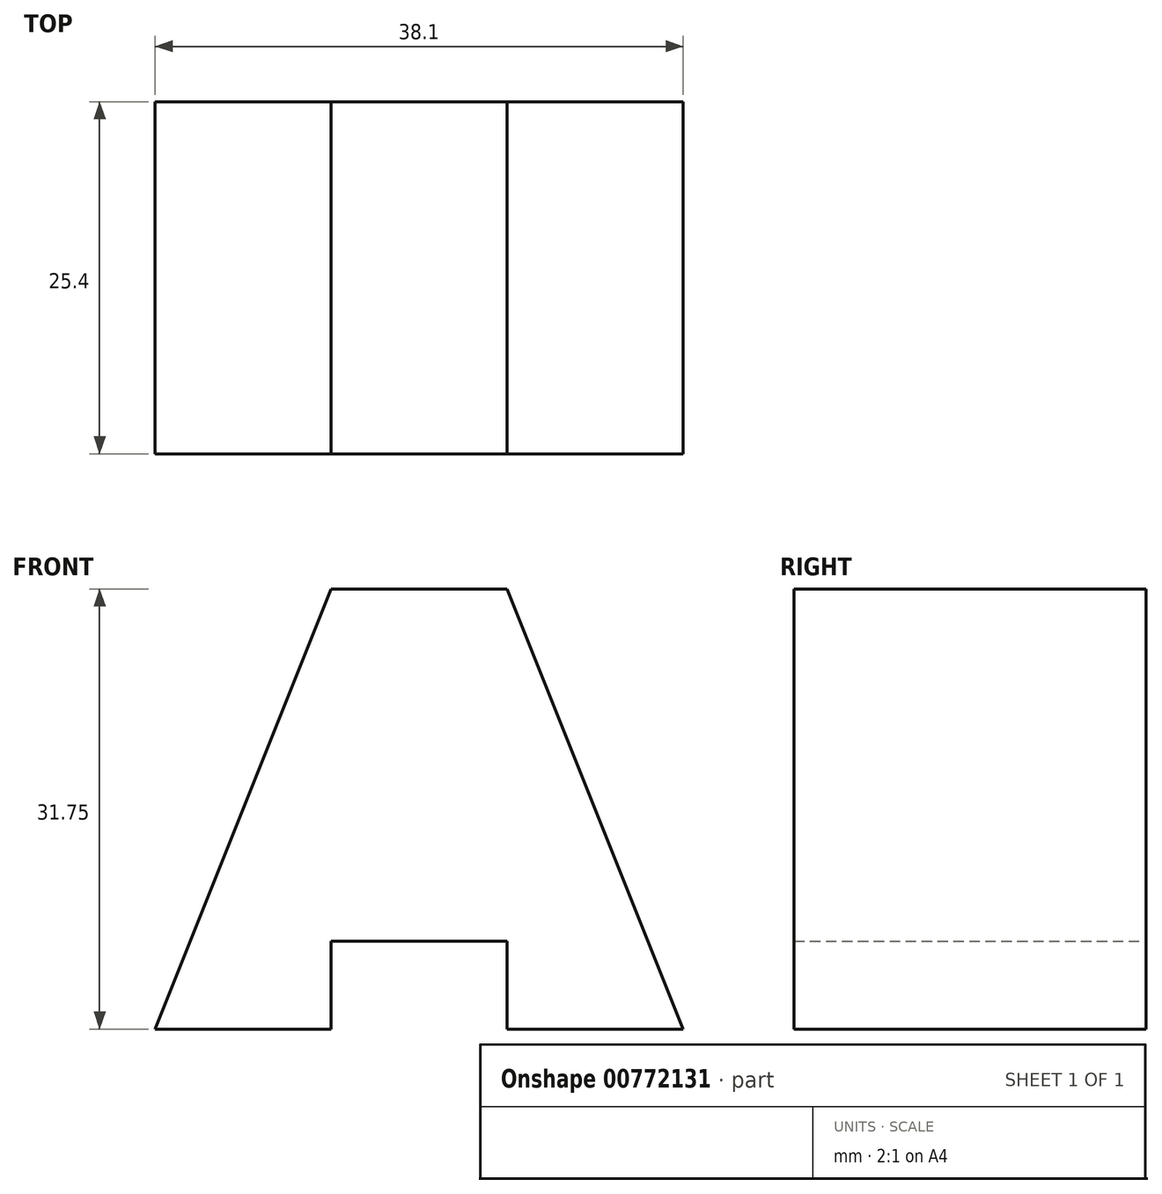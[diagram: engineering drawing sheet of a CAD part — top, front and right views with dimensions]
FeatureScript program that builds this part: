
annotation { "Feature Type Name" : "Feature", "Feature Type Description" : "" }
export const myFeature = defineFeature(function(context is Context, id is Id, definition is map)
    precondition{}
    {
        {
            var Q0;
            Q0=qCreatedBy(makeId("Front.planeOp"),FACE);
            var sketch = newSketch(context, id + "F0", { "sketchPlane" : qUnion([Q0])});
            skLineSegment(sketch, "E0", {"start": v(0, 0) * mm, "end": v(0, -6.35) * mm});
            skLineSegment(sketch, "E1", {"start": v(0, -6.35) * mm, "end": v(-12.7, -6.35) * mm});
            skLineSegment(sketch, "E2", {"start": v(0, 0) * mm, "end": v(12.7, 0) * mm});
            skLineSegment(sketch, "E3", {"start": v(12.7, 0) * mm, "end": v(12.7, -6.35) * mm});
            skLineSegment(sketch, "E4", {"start": v(12.7, -6.35) * mm, "end": v(25.4, -6.35) * mm});
            skLineSegment(sketch, "E5", {"start": v(0, 25.4) * mm, "end": v(12.7, 25.4) * mm});
            skLineSegment(sketch, "E6", {"start": v(-12.7, -6.35) * mm, "end": v(0, 25.4) * mm});
            skLineSegment(sketch, "E7", {"start": v(12.7, 25.4) * mm, "end": v(25.4, -6.35) * mm});
            skSolve(sketch);
        }
        {
            var Q0;
            Q0=makeQuery(id+"F0.imprint","IMPRINT",FACE,{"disambiguationData":[TD([[makeQuery(id+"F0.imprint","IMPRINT",EDGE,{"derivedFrom":sQuery(id+"F0.wireOp",EDGE,"E0")}),-1.0]])]});
            extrude(context, id + "F1", {"entities" : qUnion([Q0]), "depth" : 25.4 * mm, "offsetDistance" : 25.4 * mm});
        }
    });
